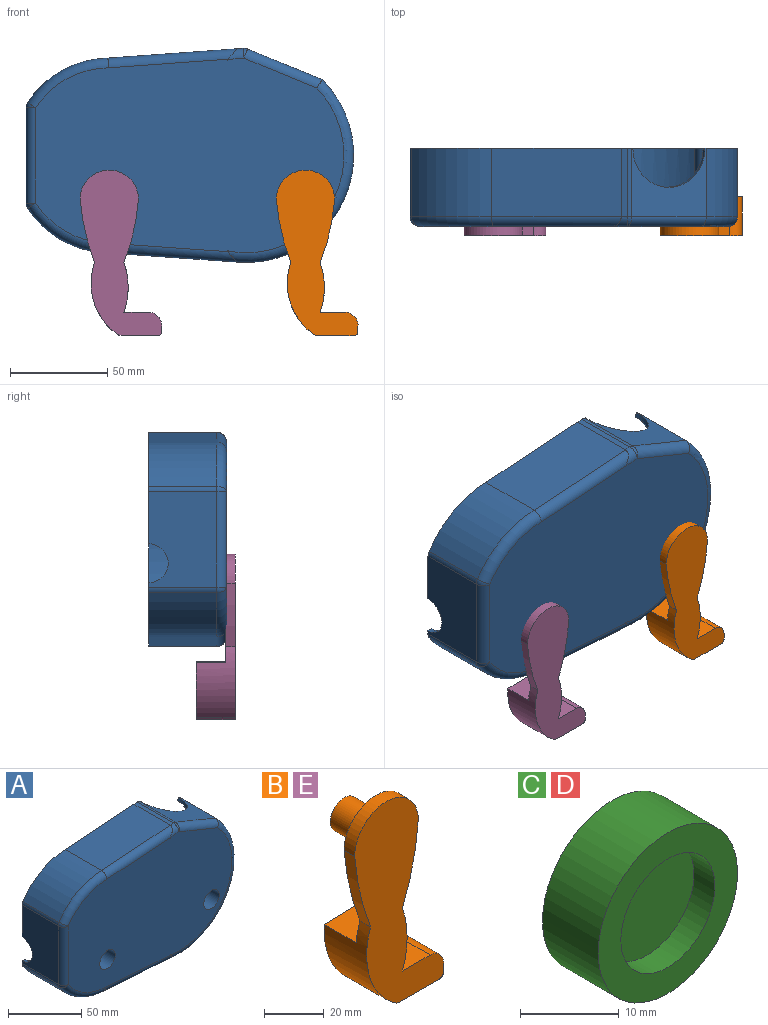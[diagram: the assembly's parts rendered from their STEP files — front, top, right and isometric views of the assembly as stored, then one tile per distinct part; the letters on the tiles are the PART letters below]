
ASSEMBLY  parts=5 mates=4
PART A: 70 faces, bbox 177.6x40x118.3 mm
  f0: plane 168.34x94.18mm, normal (0,1,0), area 626.6mm2, adj f2,f3,f4,f9,f10,f11,f13,f14
  f1: plane 114.49x57.21mm, normal (0,1,0), area 372.4mm2, adj f2,f5,f6,f7,f8,f9,f15,f16
  f2: plane 38.44x35mm, normal (0.38,0,0.93), area 825.2mm2, adj f0,f1,f4,f37,f39,f41
  f3: plane 35x0.01mm, normal (1,0,0), area 0.3mm2, adj f0,f4,f11,f33
  f4: cylinder r=55mm len=93.89mm, axis (0,-1,0), area 4706.4mm2, adj f0,f2,f3,f35
  f5: cylinder r=55mm len=35mm, axis (0,-1,0), area 115.2mm2, adj f1,f6,f36,f39
  f6: plane 35x0.01mm, normal (1,0,0), area 0.3mm2, adj f1,f5,f7,f34
  f7: plane 66.38x35mm, normal (-0.07,0,1), area 2329.2mm2, adj f1,f6,f8,f32
  f8: cylinder r=50mm len=41.28mm, axis (0,-1,0), area 1719.1mm2, adj f1,f7,f25,f30
  f9: plane 48.94x35mm, normal (-1,0,0), area 1555.9mm2, adj f0,f1,f24,f25,f26,f40
  f10: cylinder r=50mm len=39.58mm, axis (0,-1,0), area 1659.5mm2, adj f0,f11,f24,f29
  f11: plane 68.08x35mm, normal (-0.07,0,-1), area 2388.7mm2, adj f0,f3,f10,f31
  f12: plane 158.34x99.98mm, normal (0,-1,0), area 13113.7mm2, adj f26,f29,f30,f31,f32,f33,f34,f35
  f13: plane 37.5x0.13mm, normal (-1,0,0), area 4.8mm2, adj f0,f14,f22,f23
  f14: cylinder r=52.5mm len=89.27mm, axis (0,-1,0), area 4875.6mm2, adj f0,f13,f15,f23,f58,f69
  f15: plane 38.45x37.5mm, normal (-0.38,0,-0.93), area 929.5mm2, adj f0,f1,f14,f16,f23,f41
  f16: cylinder r=52.5mm len=37.5mm, axis (0,-1,0), area 240.6mm2, adj f1,f15,f17,f23
  f17: plane 37.5x0.12mm, normal (-1,0,0), area 4.7mm2, adj f1,f16,f18,f23
  f18: plane 63.77x37.5mm, normal (0.07,0,-1), area 2384.9mm2, adj f1,f17,f19,f23,f60
  f19: cylinder r=47.5mm len=39.69mm, axis (0,-1,0), area 1755mm2, adj f1,f18,f20,f23,f61
  f20: plane 50.4x37.5mm, normal (1,0,0), area 1730.8mm2, adj f0,f1,f19,f21,f23,f40,f61
  f21: cylinder r=47.5mm len=38.04mm, axis (0,-1,0), area 1718.3mm2, adj f0,f20,f22,f23
  f22: plane 65.43x37.5mm, normal (0.07,0,1), area 2442.4mm2, adj f0,f13,f21,f23,f59
  f23: plane 163.34x104.99mm, normal (0,1,0), area 11430mm2, adj f13,f14,f15,f16,f17,f18,f19,f20
  f24: cylinder r=5mm len=35mm, axis (0,-1,0), area 100.6mm2, adj f0,f9,f10,f27
  f25: cylinder r=5mm len=35mm, axis (0,-1,0), area 100.6mm2, adj f1,f8,f9,f28
  f26: cylinder r=5mm len=48.94mm, axis (0,0,-1), area 384.4mm2, adj f9,f12,f27,f28
  f27: sphere r=5mm, area 14.4mm2, adj f24,f26,f29
  f28: sphere r=5mm, area 14.4mm2, adj f25,f26,f30
  f29: torus R=45mm, axis (0,1,0), area 359.1mm2, adj f10,f12,f27,f31
  f30: torus R=45mm, axis (0,1,0), area 372.3mm2, adj f8,f12,f28,f32
  f31: cylinder r=5mm len=68.49mm, axis (1,0,-0.07), area 520.9mm2, adj f11,f12,f29,f33
  f32: cylinder r=5mm len=66.89mm, axis (-1,0,-0.07), area 507.9mm2, adj f7,f12,f30,f34
  f33: cylinder r=5mm len=5.78mm, axis (0,0,1), area 0.9mm2, adj f3,f12,f31,f35
  f34: cylinder r=5mm len=5.78mm, axis (0,0,1), area 0.8mm2, adj f6,f12,f32,f36
  f35: torus R=50mm, axis (0,1,0), area 1032.8mm2, adj f4,f12,f33,f37
  f36: torus R=50mm, axis (0,1,0), area 40.7mm2, adj f5,f12,f34,f38
  f37: cylinder r=5mm len=40.33mm, axis (-0.93,0,0.38), area 322.1mm2, adj f2,f12,f35,f38
  f38: sphere r=5mm, area 10.4mm2, adj f36,f37,f39
  f39: cylinder r=5mm len=35mm, axis (0,-1,0), area 73mm2, adj f1,f2,f5,f38
  f40: cylinder r=10mm len=20mm, axis (-1,0,0), area 78.5mm2, adj f0,f1,f9,f20
  f41: cylinder r=20mm len=37.97mm, axis (0.38,0,0.93), area 157.1mm2, adj f0,f1,f2,f15
  f42: plane 15x15mm, normal (0,1,0), area 98.2mm2, adj f43,f44
  f43: cylinder r=5mm len=37.5mm, axis (0,-1,0), area 1178.1mm2, adj f42,f45
  f44: cylinder r=7.5mm len=32.5mm, axis (0,-1,0), area 1531.5mm2, adj f42,f61
  f45: plane 10x10mm, normal (0,1,0), area 78.5mm2, adj f43
  f46: plane 15x15mm, normal (0,1,0), area 98.2mm2, adj f47,f48
  f47: cylinder r=5mm len=37.5mm, axis (0,-1,0), area 1178.1mm2, adj f46,f49
  f48: cylinder r=7.5mm len=32.5mm, axis (0,-1,0), area 1531.5mm2, adj f46,f59
  f49: plane 10x10mm, normal (0,1,0), area 78.5mm2, adj f47
  f50: plane 15x15mm, normal (0,1,0), area 98.2mm2, adj f51,f52
  f51: cylinder r=5mm len=37.5mm, axis (0,-1,0), area 1178.1mm2, adj f50,f53
  f52: cylinder r=7.5mm len=32.5mm, axis (0,-1,0), area 1531.5mm2, adj f50,f60
  f53: plane 10x10mm, normal (0,1,0), area 78.5mm2, adj f51
  f54: plane 15x15mm, normal (0,1,0), area 100.2mm2, adj f55,f56
  f55: cylinder r=4.94mm len=37.5mm, axis (0,-1,0), area 1163mm2, adj f54,f57
  f56: cylinder r=7.5mm len=32.5mm, axis (0,-1,0), area 1531.5mm2, adj f54,f58
  f57: plane 9.87x9.87mm, normal (0,1,0), area 76.5mm2, adj f55
  f58: torus R=12.5mm, axis (0,1,0), area 392.7mm2, adj f14,f23,f56
  f59: torus R=12.5mm, axis (0,1,0), area 404.1mm2, adj f22,f23,f48
  f60: torus R=12.5mm, axis (0,1,0), area 413.9mm2, adj f18,f23,f52
  f61: torus R=12.5mm, axis (0,1,0), area 377mm2, adj f19,f20,f23,f44
  f62: cylinder r=7.5mm len=15mm, axis (0,-1,0), area 589mm2, adj f12,f65
  f63: cylinder r=7.5mm len=15mm, axis (0,-1,0), area 589mm2, adj f12,f67
  f64: cylinder r=10mm len=20mm, axis (0,-1,0), area 314.2mm2, adj f65,f69
  f65: plane 20x20mm, normal (0,1,0), area 137.4mm2, adj f62,f64
  f66: cylinder r=10mm len=20mm, axis (0,-1,0), area 314.2mm2, adj f67,f68
  f67: plane 20x20mm, normal (0,1,0), area 137.4mm2, adj f63,f66
  f68: torus R=15mm, axis (0,1,0), area 583.1mm2, adj f23,f66
  f69: torus R=15mm, axis (0,1,0), area 583.1mm2, adj f14,f23,f64
PART B: 17 faces, bbox 42x20x85 mm
  f0: cylinder r=117.61mm len=32.5mm, axis (0,1,0), area 167.3mm2, adj f2,f3,f11,f14
  f1: cylinder r=106.34mm len=32.5mm, axis (0,1,0), area 167.5mm2, adj f3,f4,f11,f14
  f2: cylinder r=32.18mm len=36.51mm, axis (0,1,0), area 691.8mm2, adj f0,f10,f11,f12,f13,f14
  f3: cylinder r=15mm len=30mm, axis (0,1,0), area 235.6mm2, adj f0,f1,f11,f14
  f4: cylinder r=37.13mm len=25.5mm, axis (0,1,0), area 402.2mm2, adj f1,f5,f11,f12,f13,f14
  f5: plane 20x13.09mm, normal (0,0,1), area 261.9mm2, adj f4,f6,f11,f12
  f6: cylinder r=6.87mm len=20mm, axis (0,1,0), area 215.8mm2, adj f5,f7,f11,f12
  f7: plane 20x2.7mm, normal (1,0,0), area 54mm2, adj f6,f8,f11,f12
  f8: cylinder r=2mm len=20mm, axis (0,1,0), area 62.8mm2, adj f7,f9,f11,f12
  f9: plane 20x18.42mm, normal (0,0,-1), area 368.3mm2, adj f8,f10,f11,f12
  f10: cylinder r=5mm len=20mm, axis (0,1,0), area 64.1mm2, adj f2,f9,f11,f12
  f11: plane 85x42.01mm, normal (0,-1,0), area 1913.1mm2, adj f0,f1,f2,f3,f4,f5,f6,f7
  f12: plane 36.35x29.85mm, normal (0,1,0), area 637.4mm2, adj f2,f4,f5,f6,f7,f8,f9,f10
  f13: plane 18.64x15mm, normal (-0.03,0,1), area 279.7mm2, adj f2,f4,f12,f14
  f14: plane 55.63x30mm, normal (0,1,0), area 1143mm2, adj f0,f1,f2,f3,f4,f13,f15
  f15: cylinder r=6.5mm len=15mm, axis (0,-1,0), area 612.6mm2, adj f14,f16
  f16: plane 13x13mm, normal (0,1,0), area 132.7mm2, adj f15
PART C: 5 faces, bbox 20x8x20 mm
  f0: cylinder r=10mm len=20mm, axis (0,1,0), area 502.7mm2, adj f1,f2
  f1: plane 20x20mm, normal (0,-1,0), area 171mm2, adj f0,f3
  f2: plane 20x20mm, normal (0,1,0), area 314.2mm2, adj f0
  f3: cylinder r=6.75mm len=13.5mm, axis (0,-1,0), area 127.2mm2, adj f1,f4
  f4: plane 13.5x13.5mm, normal (0,-1,0), area 143.1mm2, adj f3
PART D: same geometry as C
PART E: same geometry as B
PLACE A t=(-83.82,-14.31,-142.5)mm
PLACE B t=(-48.74,1.19,-173.81)mm
PLACE C t=(-93.64,6.19,-169.72)mm
PLACE D t=(-194.42,6.19,-169.72)mm
PLACE E t=(-149.52,1.19,-173.81)mm
MATE fastened D.f0 <-> A.f63  axis (0,-1,0) through (-149.52,-1.81,-165.05)mm
MATE fastened E.f15 <-> D.f0  axis (0,1,0) through (-149.52,1.19,-165.05)mm
MATE fastened A.f62 <-> C.f0  axis (0,1,0) through (-48.74,-1.81,-165.05)mm
MATE fastened C.f0 <-> B.f15  axis (0,-1,0) through (-48.74,1.19,-165.05)mm
